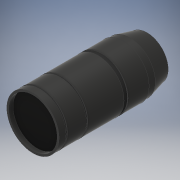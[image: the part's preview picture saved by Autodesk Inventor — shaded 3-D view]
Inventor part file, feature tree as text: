
AUTODESK INVENTOR PART (.ipt)
format: ipt  version: 2019 (Build 230136000, 136)  size: 169,984 bytes
history: native  units: mm
features: extrude x9, sketch x9, projected_geometry x6, chamfer x1
ambient origin geometry x8: Origin, YZ Plane, XZ Plane, XY Plane, X Axis, Y Axis, Z Axis, Center Point
bodies: Solid1 (feature_tree)
feature tree (25):
  extrude  "Extrusion1"  Depth=16.8mm TaperAngle=0.0deg
  extrude  "Extrusion2"  Depth=14.7mm TaperAngle=0.0deg
  chamfer  "Chamfer1"  Distance=3.0mm Angle=45.0deg
  extrude  "Extrusion3"  Depth=2.8mm TaperAngle=0.0deg
  extrude  "Extrusion4"  Depth=25.25mm TaperAngle=0.0deg
  extrude  "Extrusion5"  Depth=1.0mm TaperAngle=0.0deg
  extrude  "Extrusion6"  Depth=13.2mm TaperAngle=0.0deg
  extrude  "Extrusion7"  Depth=1.0mm TaperAngle=0.0deg
  extrude  "Extrusion8"  Depth=4.85mm TaperAngle=0.0deg
  extrude  "Extrusion9"  [1 undecoded]
  sketch  "Sketch1"  dims[d0=35.5mm d1=16.8mm d2=0.0mm]
  sketch  "Sketch2"  dims[d3=36.5mm d4=14.7mm d5=0.0mm d6=3.0mm d7=12.0mm d8=45.0deg]
  projected_geometry  "Projected Loop1"
  sketch  "Sketch3"  dims[d9=35.5mm d10=2.8mm d11=0.0mm]
  projected_geometry  "Projected Loop2"
  sketch  "Sketch4"  dims[d12=36.5mm d13=25.25mm d14=0.0mm]
  projected_geometry  "Projected Loop3"
  sketch  "Sketch5"  dims[d15=35.5mm d16=1.0mm d17=0.0mm]
  projected_geometry  "Projected Loop4"
  sketch  "Sketch6"  dims[d18=36.5mm d19=13.2mm d20=0.0mm]
  sketch  "Sketch7"  dims[d21=35.5mm d22=1.0mm d23=0.0mm]
  projected_geometry  "Projected Loop5"
  sketch  "Sketch8"  dims[d24=36.5mm d25=4.85mm d26=0.0mm]
  projected_geometry  "Projected Loop6"
  sketch  "Sketch9"  dims[d27=3.0mm d28=0.0mm]
note: 1 required parameter value undecoded (feature->parameter linkage not recoverable at this tier; creation-order binding heuristic only, values carry confidence <= 0.55)
